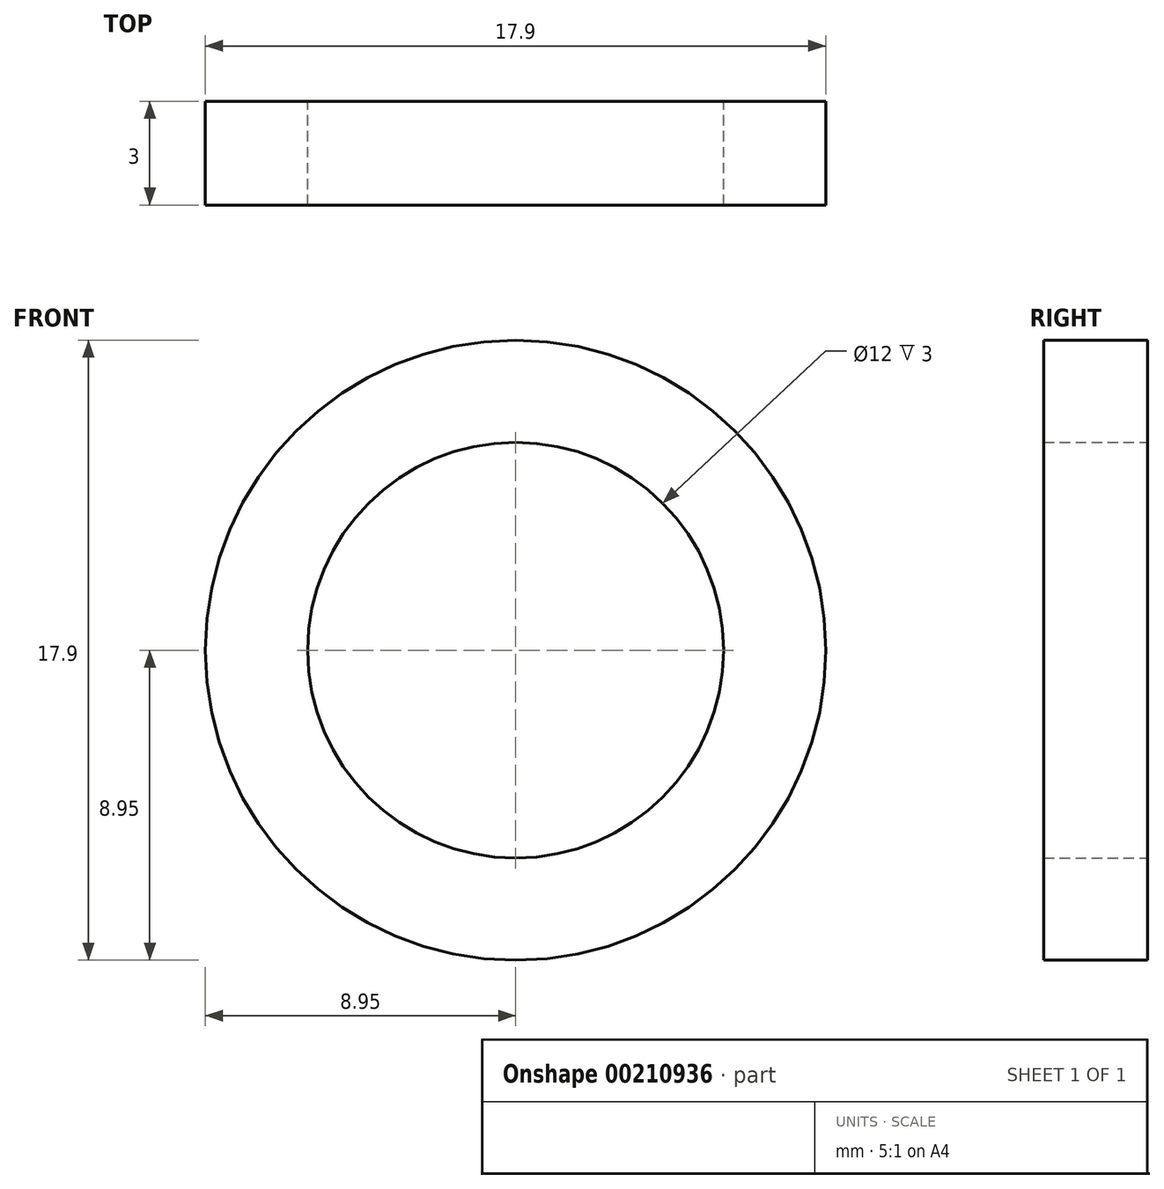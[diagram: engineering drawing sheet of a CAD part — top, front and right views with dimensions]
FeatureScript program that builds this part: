
annotation { "Feature Type Name" : "Feature", "Feature Type Description" : "" }
export const myFeature = defineFeature(function(context is Context, id is Id, definition is map)
    precondition{}
    {
        {
            var Q0;
            Q0=qCreatedBy(makeId("Front.planeOp"),FACE);
            var sketch = newSketch(context, id + "F0", { "sketchPlane" : qUnion([Q0])});
            skCircle(sketch, "E0", {"center": v(0, 0) * mm, "radius": 8.95 * mm});
            skCircle(sketch, "E1", {"center": v(0, 0) * mm, "radius": 6 * mm});
            skSolve(sketch);
        }
        {
            var Q0;
            Q0=makeQuery(id+"F0.imprint","IMPRINT",FACE,{"disambiguationData":[TD([[makeQuery(id+"F0.imprint","IMPRINT",EDGE,{"derivedFrom":sQuery(id+"F0.wireOp",EDGE,"E0")}),1.0]])]});
            extrude(context, id + "F1", {"entities" : qUnion([Q0]), "depth" : 3 * mm});
        }
    });
